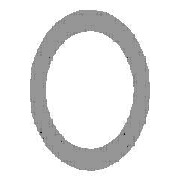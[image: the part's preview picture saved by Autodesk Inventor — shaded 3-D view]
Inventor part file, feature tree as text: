
AUTODESK INVENTOR PART (.ipt)
format: ipt  version: 2013 (Build 170138000, 138)  size: 125,440 bytes
history: native  units: mm (DEFAULTED — no unit token found)
features: plane x7, sketch x5, other x4, extrude x2
ambient origin geometry x8: Origin, YZ Plane, XZ Plane, XY Plane, X Axis, Y Axis, Z Axis, Center Point
bodies: Solid1 (feature_tree), Body (feature_tree)
feature tree (18):
  parser-record x1  (decoder bookkeeping rows leaked as tree rows — omitted from the tree; the rows remain in map.json)
  other  "Driven Length"
  other  "Start plane"
  other  "End plane"
  plane  "Work Plane4"
  plane  "Work Plane5"
  plane  "Work Plane6"
  extrude  "Extrusion2"  Depth=3.3782mm
  plane  "Work Plane7"
  plane  "Work Plane8"
  plane  "Work Plane9"
  extrude  "Extrusion3"  TaperAngle=0.0deg  [1 undecoded]
  sketch  "Sketch"  dims[d7=406.4mm d8=3.302mm d9=0.0mm d10=3.302mm d11=0.0mm]
  sketch  "Sketch3"  dims[d0=33.401mm d1=3.3782mm]
  plane  "Work Plane3"
  sketch  "Sketch4"  dims[d2=406.4mm d3=0.0mm d4=-0.0mm]
  sketch  "Sketch5"  dims[d5=406.4mm]
  sketch  "Sketch6"  dims[d6=90.0deg]
note: 1 required parameter value undecoded (feature->parameter linkage not recoverable at this tier; creation-order binding heuristic only, values carry confidence <= 0.55)
